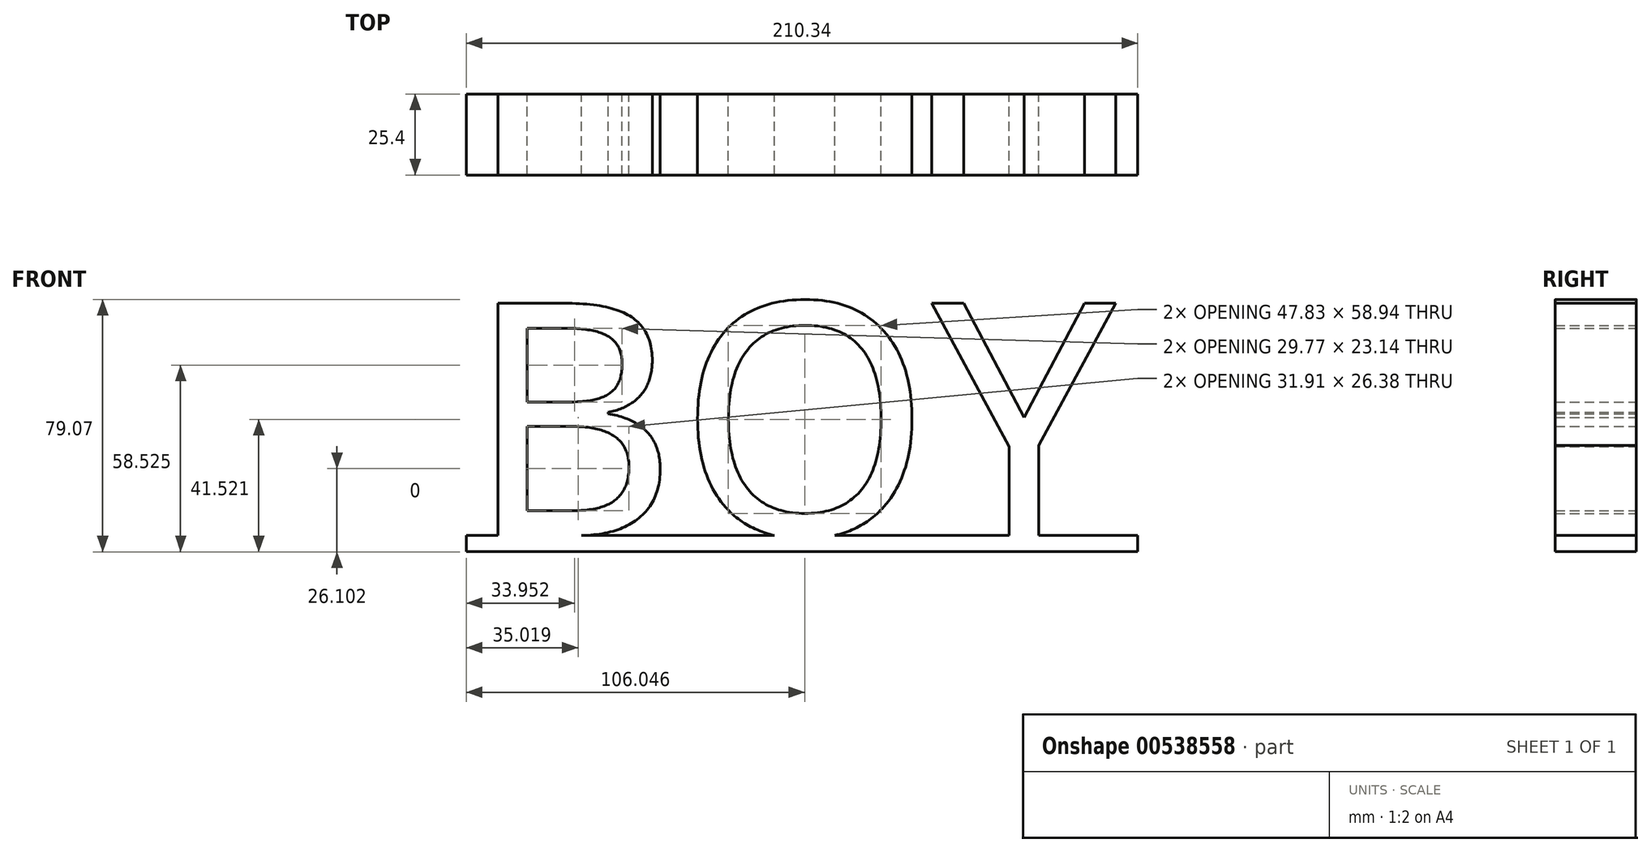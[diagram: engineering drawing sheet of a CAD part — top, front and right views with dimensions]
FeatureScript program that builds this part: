
annotation { "Feature Type Name" : "Feature", "Feature Type Description" : "" }
export const myFeature = defineFeature(function(context is Context, id is Id, definition is map)
    precondition{}
    {
        {
            var Q0;
            Q0=qCreatedBy(makeId("Front.planeOp"),FACE);
            var sketch = newSketch(context, id + "F0", { "sketchPlane" : qUnion([Q0])});
            skText(sketch, "E0", { "text": "BOY", "fontName": "NotoSans-Regular.ttf"});
            skLineSegment(sketch, "E1.bottom", {"start": v(-97.63, -32.79) * mm, "end": v(112.7, -32.79) * mm});
            skLineSegment(sketch, "E1.top", {"start": v(-97.63, -37.93) * mm, "end": v(112.7, -37.93) * mm});
            skLineSegment(sketch, "E1.left", {"start": v(-97.63, -32.79) * mm, "end": v(-97.63, -37.93) * mm});
            skLineSegment(sketch, "E1.right", {"start": v(112.7, -32.79) * mm, "end": v(112.7, -37.93) * mm});
            const initialGuessF0  = {"E0": [-0.09763, -0.03279, 1, 0, 0.0734]};
            skSetInitialGuess(sketch, initialGuessF0);
            skSolve(sketch);
        }
        {
            var Q0;
            Q0 = qSketchRegion(id + "F0", true);
            extrude(context, id + "F1", {"entities" : qUnion([Q0]), "depth" : 25.4 * mm, "offsetDistance" : 25.4 * mm});
        }
    });
